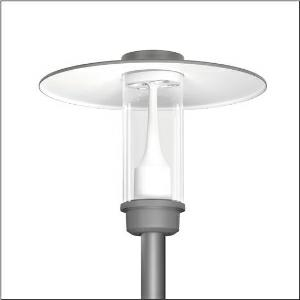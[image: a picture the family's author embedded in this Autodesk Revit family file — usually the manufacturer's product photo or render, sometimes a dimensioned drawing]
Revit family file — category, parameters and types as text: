
# Revit family: litepole_2_iq___pl1_2s_5xa5425cf14h_8640
name_source: partatom
category: Lighting Fixtures
units: mm (PartAtom-declared; Revit-internal decimal feet)

## family parameters
Cut with Voids When Loaded = No
Host = Face
Light Source = No
Part Type = Normal
Room Calculation Point = No
Round Connector Dimension = Use Diameter
Shared = No

## types (1)
- --- (1 x LED, 2990 lm, 23.9 W, 2200K)
    Apparent Load = 24 VA
    CIE Flux Codes = 22 60 92 98 100
    Color Rendering = 70
    Color Temperature = 2200K
    Default Elevation = 1800 mm
    Description = Litepole 2 iQ, mast luminaire, Module 540 iQ-SR, primary light control with 3 zone facetted reflector, of plastic, silver coated, highly specular, structured, primary optical cover: cover, of PMMA, transparent, light distribution: PL1.2s, light emission: direct distribution, primary light characteristic: symmetric, installation type: post-top, LED, High Power LED, rated luminous flux: 2.990lm, luminous efficacy: 125lm/W, light colour: 722, colour temperature: 2200K, control gear: iQ Street-Remote, control: pre-setting: logarithmic dimming characteristic, Street-Remote, Auto-Match, Temp-Guard, Lumen-Switch, Night-Set, Smart-Wire, Light-Fading, Desk-Remote (wireless, voltage-free reading and setting of iQ features in the workshop via application-optimized NFC function/RFID function), optimised constant luminous flux control (CLO 2.0), with terminal, 6-pole, max. 2.5mm², mains connection: 230..240V, AC, 50/60Hz, start of lifetime: 24W, end of service life: 26W, reduction: 12W, luminaire housing, upper part, of aluminium, coated, Siteco® metallic grey (DB 702S), diameter: 750mm, height: 590mm, spigot size: d x l = 76 x 70mm (post-top) | with reducer (optional accessory) 60 x 70mm, mounting height: 3..5m, post-top mast mounting element, of diecast aluminium, coated, Siteco® metallic grey (DB 702S), Module 540 iQ-SR, traffic white (RAL 9016), equipment: standard, protection rating (complete): IP65, insulation class (complete): insulation class II (safety insulation), certification: CE, ENEC, VDE, packaging unit: 1 piece

Light Distribution: PL1.2s
    Height = 590 mm
    Lamp = 1 x LED
    Lamp Light Flux = 2990 lm
    Lamp Power = 23.9 W
    Lamp count = 1
    Length = 750 mm
    Luminous efficacy = 125 lm/W
    Manufacturer = Siteco
    ModVariant = No
    Model = 5XA5425CF14H
    Number of Poles = 1
    OnlyDefault = Yes
    Power Factor = 1
    Product Name = Litepole 2 iQ | PL1.2s
    Product group = mast luminaire | pylon top
    ProductGroupID = 6100
    Protection Class = Protection class II
    Protection Degree = IP 65
    RLX_Detail_Level = 1
    RLX_Emergency_Light_Flux = 0 lm
    RLX_Emergency_Type = 0
    RLX_Emergency_Type_DB = No
    RlxData = <blob elided: 29501 chars, md5=44f65f43>
    Socket = socket
    Standby Power = 0 W
    System Light Flux = 2990 lm
    System Power = 24 W
    Type Comments = factory setting: luminous flux: 100 % | dim-lin: 254 | 499 mA
    Type Image = l_1006518.jpg
    URL = http://relux.com
    VarID = @adj_166161
    Voltage = 0 V
    Weight = 0.00 kg
    Width = 0 mm  [stored 0 ft]

note: [stored X ft] marks values corroborated as IEEE doubles in the binary element streams (Revit-internal decimal feet)

## geometry (parser evidence)
native form markers: Blend x4, Sweep x10
no freeform markers — native parametric forms only
